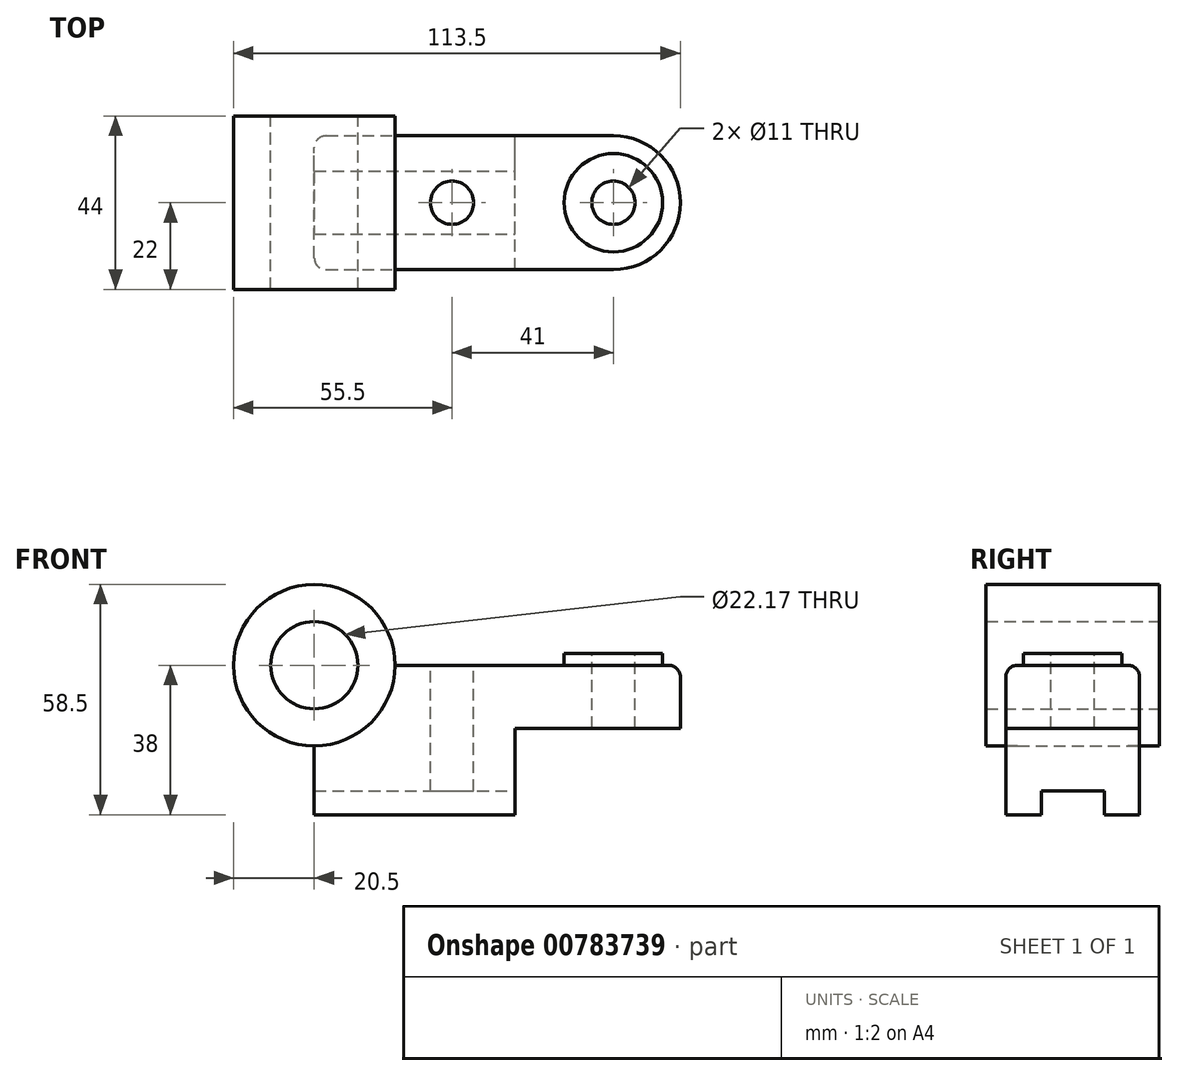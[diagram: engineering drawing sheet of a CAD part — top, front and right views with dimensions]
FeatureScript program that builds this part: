
annotation { "Feature Type Name" : "Feature", "Feature Type Description" : "" }
export const myFeature = defineFeature(function(context is Context, id is Id, definition is map)
    precondition{}
    {
        {
            var Q0;
            Q0=qCreatedBy(makeId("Front.planeOp"),FACE);
            var sketch = newSketch(context, id + "F0", { "sketchPlane" : qUnion([Q0])});
            skLineSegment(sketch, "E0.bottom", {"start": v(0, 0) * mm, "end": v(51, 0) * mm});
            skLineSegment(sketch, "E0.top", {"start": v(0, 38) * mm, "end": v(76, 38) * mm});
            skLineSegment(sketch, "E0.left", {"start": v(0, 0) * mm, "end": v(0, 38) * mm});
            skLineSegment(sketch, "E0.right", {"start": v(76, 22) * mm, "end": v(76, 38) * mm});
            skLineSegment(sketch, "E1.top", {"start": v(51, 22) * mm, "end": v(76, 22) * mm});
            skLineSegment(sketch, "E1.left", {"start": v(51, 0) * mm, "end": v(51, 22) * mm});
            skCircle(sketch, "E2", {"center": v(0, 38) * mm, "radius": 11.09 * mm});
            skCircle(sketch, "E3", {"center": v(0, 38) * mm, "radius": 20.5 * mm});
            skSolve(sketch);
        }
        {
            var Q0;
            {var subQ2=sQuery(id+"F0.wireOp",EDGE,"E0.bottom");Q0=makeQuery(id+"F0.imprint","IMPRINT",FACE,{"disambiguationData":[TD([[makeQuery(id+"F0.imprint","IMPRINT",EDGE,{"derivedFrom":subQ2}),1.0]])]});}
            extrude(context, id + "F1", {"entities" : qUnion([Q0]), "endBound" : BoundingType.SYMMETRIC, "depth" : (17 * 2) * mm});
        }
        {
            var Q0;
            {var subQ0=sQuery(id+"F0.wireOp",EDGE,"E3");var subQ1=sQuery(id+"F0.wireOp",EDGE,"E0.top");var subQ2=makeQuery(id+"F0.imprint","INTERSECT",VERTEX,{"derivedFrom":[subQ1,subQ0]});Q0=makeQuery(id+"F0.imprint","IMPRINT",FACE,{"disambiguationData":[TD([[makeQuery(id+"F0.imprint","IMPRINT",EDGE,{"disambiguationData":[TD([[subQ2,1.0]])],"derivedFrom":subQ1}),1.0]])]});}
            var Q1;
            {var subQ0=sQuery(id+"F0.wireOp",EDGE,"E3");var subQ1=sQuery(id+"F0.wireOp",EDGE,"E0.top");var subQ2=makeQuery(id+"F0.imprint","INTERSECT",VERTEX,{"derivedFrom":[subQ1,subQ0]});Q1=makeQuery(id+"F0.imprint","IMPRINT",FACE,{"disambiguationData":[TD([[makeQuery(id+"F0.imprint","IMPRINT",EDGE,{"disambiguationData":[TD([[subQ2,1.0]])],"derivedFrom":subQ1}),-1.0]])]});}
            extrude(context, id + "F2", {"entities" : qUnion([Q0, Q1]), "operationType" : NewBodyOperationType.ADD, "endBound" : BoundingType.SYMMETRIC, "depth" : 44 * mm});
        }
        {
            var Q0;
            Q0=makeQuery(id+"F1.opExtrude","SWEPT_FACE",FACE,{"disambiguationData":[OSD([sQuery(id+"F0.wireOp",EDGE,"E0.top")])]});
            var sketch = newSketch(context, id + "F3", { "sketchPlane" : qUnion([Q0])});
            skArc(sketch, "E4", {"start": v(76, -17) * mm, "mid": v(93, 0) * mm, "end": v(76, 17) * mm});
            skSolve(sketch);
        }
        {
            var Q0;
            Q0=makeQuery(id+"F3.imprint","IMPRINT",FACE,{"disambiguationData":[TD([[makeQuery(id+"F3.imprint","IMPRINT",EDGE,{"derivedFrom":sQuery(id+"F3.wireOp",EDGE,"E4")}),1.0]])]});
            var Q1;
            Q1=makeQuery(id+"F1.opExtrude","SWEPT_FACE",FACE,{"disambiguationData":[OSD([sQuery(id+"F0.wireOp",EDGE,"E1.top")])]});
            extrude(context, id + "F4", {"entities" : qUnion([Q0]), "operationType" : NewBodyOperationType.ADD, "endBound" : BoundingType.UP_TO_SURFACE, "oppositeDirection" : true, "endBoundEntityFace" : qUnion([Q1]), "depth" : 25 * mm});
        }
        {
            var Q0;
            {var subQ0=sQuery(id+"F0.wireOp",EDGE,"E0.top");Q0=makeQuery(id+"F4.boolean.opBoolean","MERGE",FACE,{"derivedFrom":[makeQuery(id+"F1.opExtrude","SWEPT_FACE",FACE,{"disambiguationData":[OSD([subQ0])]}),makeQuery(id+"F4.opExtrude","CAP_FACE",FACE,{"disambiguationData":[OSD([subQ0,sQuery(id+"F0.wireOp",EDGE,"E0.right"),sQuery(id+"F3.wireOp",EDGE,"E4")])],"isStart":true})]});}
            var sketch = newSketch(context, id + "F5", { "sketchPlane" : qUnion([Q0])});
            skCircle(sketch, "E5", {"center": v(76, 0) * mm, "radius": 12.5 * mm});
            skSolve(sketch);
        }
        {
            var Q0;
            Q0=makeQuery(id+"F5.imprint","IMPRINT",FACE,{"disambiguationData":[TD([[makeQuery(id+"F5.imprint","IMPRINT",EDGE,{"derivedFrom":sQuery(id+"F5.wireOp",EDGE,"E5")}),1.0]])]});
            extrude(context, id + "F6", {"entities" : qUnion([Q0]), "operationType" : NewBodyOperationType.ADD, "depth" : 3 * mm});
        }
        {
            var Q0;
            Q0=makeQuery(id+"F6.opExtrude","CAP_FACE",FACE,{"disambiguationData":[OSD([sQuery(id+"F5.wireOp",EDGE,"E5")])],"isStart":false});
            var sketch = newSketch(context, id + "F7", { "sketchPlane" : qUnion([Q0])});
            skCircle(sketch, "E6", {"center": v(76, 0) * mm, "radius": 5.5 * mm});
            skCircle(sketch, "E7", {"center": v(35, 0) * mm, "radius": 5.5 * mm});
            skSolve(sketch);
        }
        {
            var Q0;
            Q0=qSketchRegion(id+"F7",true);
            extrude(context, id + "F8", {"entities" : qUnion([Q0]), "operationType" : NewBodyOperationType.REMOVE, "endBound" : BoundingType.THROUGH_ALL, "oppositeDirection" : true, "depth" : 25 * mm});
        }
        {
            var Q0;
            Q0=makeQuery(id+"F1.opExtrude","SWEPT_FACE",FACE,{"disambiguationData":[OSD([sQuery(id+"F0.wireOp",EDGE,"E1.left")])]});
            var sketch = newSketch(context, id + "F9", { "sketchPlane" : qUnion([Q0])});
            skLineSegment(sketch, "E8.bottom", {"start": v(-8, 0) * mm, "end": v(8, 0) * mm});
            skLineSegment(sketch, "E8.top", {"start": v(-8, 6) * mm, "end": v(8, 6) * mm});
            skLineSegment(sketch, "E8.left", {"start": v(-8, 0) * mm, "end": v(-8, 6) * mm});
            skLineSegment(sketch, "E8.right", {"start": v(8, 0) * mm, "end": v(8, 6) * mm});
            skSolve(sketch);
        }
        {
            var Q0;
            Q0=qSketchRegion(id+"F9",true);
            extrude(context, id + "F10", {"entities" : qUnion([Q0]), "operationType" : NewBodyOperationType.REMOVE, "endBound" : BoundingType.THROUGH_ALL, "oppositeDirection" : true, "depth" : 25 * mm});
        }
        {
            var Q0;
            Q0=makeQuery(id+"F6.opExtrude","CAP_EDGE",EDGE,{"disambiguationData":[OSD([sQuery(id+"F5.wireOp",EDGE,"E5")])],"isStart":true});
            var Q1;
            Q1=makeQuery(id+"F1.opExtrude","CAP_EDGE",EDGE,{"disambiguationData":[OSD([sQuery(id+"F0.wireOp",EDGE,"E3")])],"isStart":false});
            var Q2;
            Q2=makeQuery(id+"F1.opExtrude","CAP_EDGE",EDGE,{"disambiguationData":[OSD([sQuery(id+"F0.wireOp",EDGE,"E3")])],"isStart":true});
            var Q3;
            Q3=makeQuery(id+"F1.opExtrude","SWEPT_EDGE",EDGE,{"disambiguationData":[OSD([sQuery(id+"F0.wireOp",EDGE,"E0.left"),sQuery(id+"F0.wireOp",EDGE,"E3")])]});
            var Q4;
            Q4=makeQuery(id+"F1.opExtrude","SWEPT_EDGE",EDGE,{"disambiguationData":[OSD([sQuery(id+"F0.wireOp",EDGE,"E0.top"),sQuery(id+"F0.wireOp",EDGE,"E3")])]});
            var Q5;
            Q5=makeQuery(id+"F1.opExtrude","CAP_EDGE",EDGE,{"disambiguationData":[OSD([sQuery(id+"F0.wireOp",EDGE,"E0.left")])],"isStart":false});
            var Q6;
            Q6=makeQuery(id+"F1.opExtrude","CAP_EDGE",EDGE,{"disambiguationData":[OSD([sQuery(id+"F0.wireOp",EDGE,"E0.left")])],"isStart":true});
            fillet(context, id + "F11", {"entities" : qUnion([Q0, Q1, Q2, Q3, Q4, Q5, Q6]), "radius" : 3 * mm, "tangentPropagation" : true, "allowEdgeOverflow" : false});
        }
        {
            var Q0;
            Q0=makeQuery(id+"F1.opExtrude","CAP_EDGE",EDGE,{"disambiguationData":[OSD([sQuery(id+"F0.wireOp",EDGE,"E0.top")])],"isStart":false});
            fillet(context, id + "F12", {"entities" : qUnion([Q0]), "radius" : 3 * mm, "tangentPropagation" : true, "allowEdgeOverflow" : false});
        }
    });
